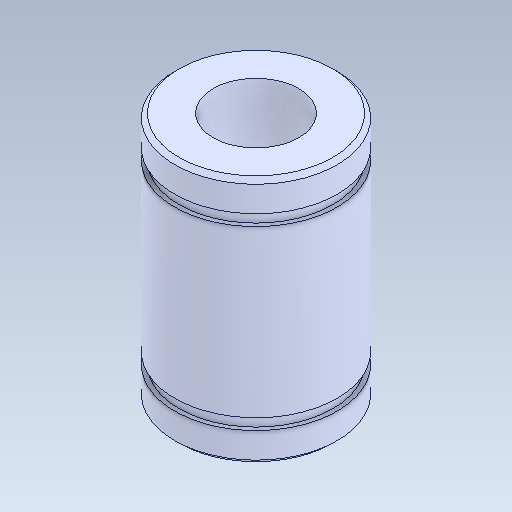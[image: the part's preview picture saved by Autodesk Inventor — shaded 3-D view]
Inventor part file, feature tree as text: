
AUTODESK INVENTOR PART (.ipt)
format: ipt  version: 2020 (Build 240168000, 168)  size: 144,384 bytes
history: native  units: in
note: dims shown in document units (in); Inventor stores cm internally (conversion verified against a paired STEP export)
features: chamfer x1
ambient origin geometry x8: Origin, YZ Plane, XZ Plane, XY Plane, X Axis, Y Axis, Z Axis, Center Point
bodies: Solid1 (feature_tree)
feature tree (1):
  chamfer  "Chamfer1"  [1 undecoded]
note: 1 required parameter value undecoded (feature->parameter linkage not recoverable at this tier; creation-order binding heuristic only, values carry confidence <= 0.55)
